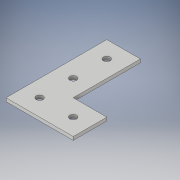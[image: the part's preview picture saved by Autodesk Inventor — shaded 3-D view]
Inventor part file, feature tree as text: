
AUTODESK INVENTOR PART (.ipt)
format: ipt  version: 2018 (Build 220112000, 112)  size: 117,760 bytes
history: native  units: in
note: dims shown in document units (in); Inventor stores cm internally (conversion verified against a paired STEP export)
features: extrude x1, sketch x1
ambient origin geometry x8: Origin, YZ Plane, XZ Plane, XY Plane, X Axis, Y Axis, Z Axis, Center Point
bodies: Solid1 (feature_tree)
feature tree (2):
  extrude  "Extrusion1"  Depth=1.0in
  sketch  "Sketch1"  dims[d0=3.0in d1=1.0in d2=1.0in d3=1.0in d5=1.5in d7=1.0in d8=1.0in d11=0.5in d12=0.5in d13=0.5in d14=0.2031in d15=0.2031in d16=0.2031in d17=0.2031in d18=0.5in d19=1.0in d20=0.5in d21=0.1in d22=0.0in]
